# Revit family: I-P65
name_source: partatom
category: Lighting Fixtures
revit_build: Autodesk Revit MEP 2012 (Build: 20110916_2132(x64)
units: mm (PartAtom-declared; Revit-internal decimal feet)

## types (4) — shared parameters
Apparent Load = 7 VA
Body Material = Eaton – (Body, Polycarbonate, RAL7035)
Circuit Watts = 5 W
Color Filter = 16777215
Diffuser Material = Eaton – (Diffuser, Polycarbonate, Clear)
Dimming Lamp Color Temperature Shift = <None>
Emergency = Yes
IP Rating = IP65
LOR = 1
Lamp = LED
Length = 263 mm  [stored 0.862861 ft]
Manufacturer = EATON
Model = IP65 LED BULKHEAD
Power Factor = 0.7
Tilt Angle = -90.00°
URL = http://www.cooper-ls.com
Voltage = 230 V
Wattage Comments = LED
Width = 142 mm  [stored 0.465879 ft]
zero-valued in all types: Default Elevation

## per-type parameters (varying)
| type | Bulkhead | Description | Double side legend panel | Exit | Height | IP65DBLLEG7010 | IP65LEG7010 | Legend | Photometric Web File | Single side legend panel | Special Considerations 1 | Special Considerations 2 | Special Considerations 3 | Weight |
| IP65LEDE3H | Yes | IP65 LED Surface mounted 2W LED emergency escape route luminaire | No | No | 55 mm  [stored 0.180446 ft] | No | No | No | IP65LEDE.IES | Yes | Legends available | Can be supplied to operate with CBU/CEAG System | Low temperature battery heater available | 0.7 |
| IP65LEDO3H | Yes | IP65 LED Surface mounted 2W LED emergency open area luminaire | No | No | 55 mm  [stored 0.180446 ft] | No | No | No | IP65LEDO.IES | Yes | Legends available | Can be supplied to operate with CBU/CEAG System | Low temperature battery heater available | 0.7 |
| IP65LEDEX3H + IP65DBLLEG7010 | No | IP65 LED Surface mounted 2W LED emergency double sided escape luminaire | Yes | Yes | 165 mm | Yes | No | Yes | IP65LEDO.IES | No | Can be supplied to operate with CBU/CEAG System | Low temperature battery heater available |  | 1.3 |
| IP65LEDO3H + IP65LEG7010 | No | IP65 LED Surface mounted 2W LED emergency open area luminaire. with Legend | No | Yes | 55 mm  [stored 0.180446 ft] | No | Yes | Yes | IP65LEDO.IES | Yes | Can be supplied to operate with CBU/CEAG System | Low temperature battery heater available |  | 0.8 |

note: column(s) folded — value = type name in every type: Part No.

note: [stored X ft] marks values corroborated as IEEE doubles in the binary element streams (Revit-internal decimal feet)

## geometry (parser evidence)
native form markers: Sweep x7
no freeform markers — native parametric forms only
